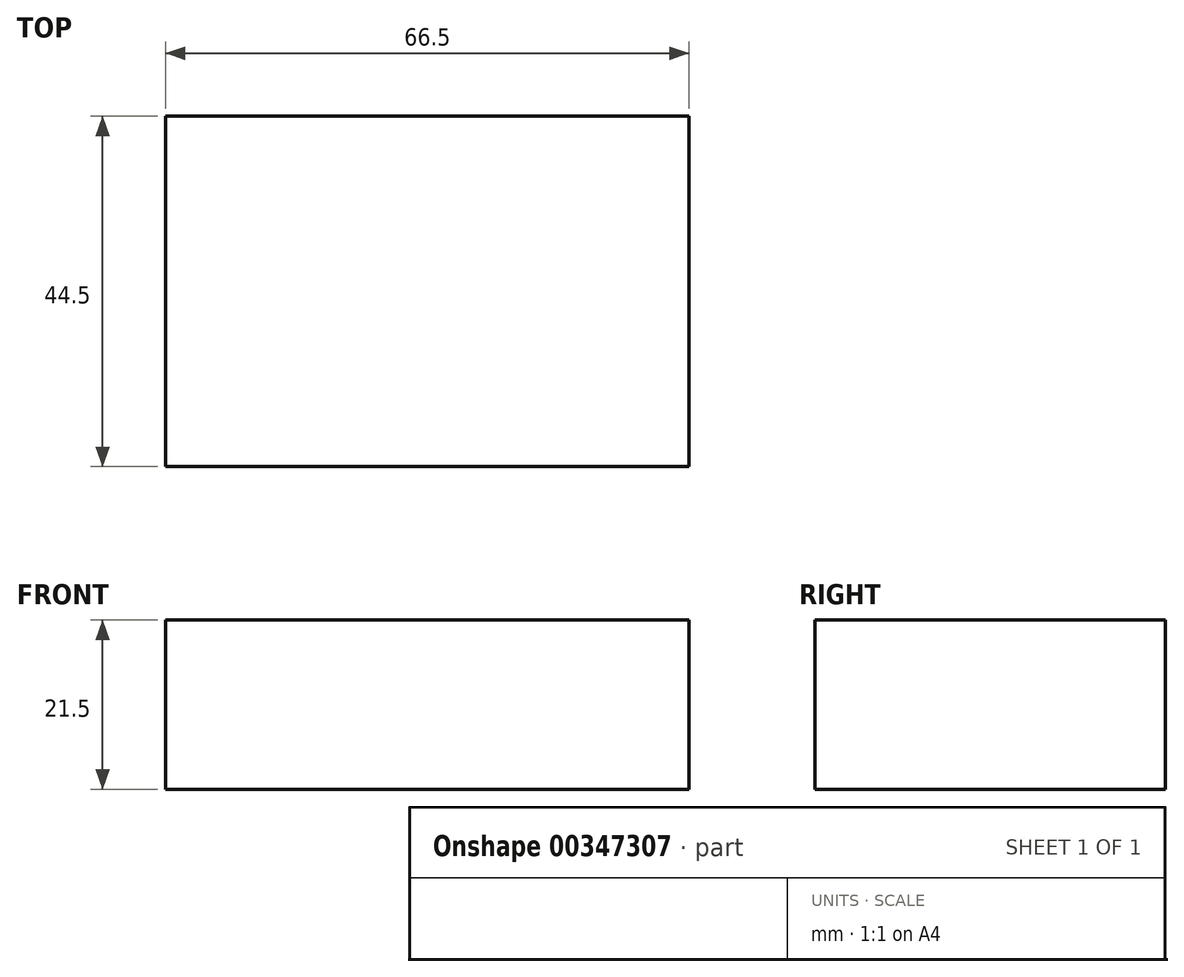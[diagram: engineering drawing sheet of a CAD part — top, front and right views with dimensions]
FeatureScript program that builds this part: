
annotation { "Feature Type Name" : "Feature", "Feature Type Description" : "" }
export const myFeature = defineFeature(function(context is Context, id is Id, definition is map)
    precondition{}
    {
        {
            var Q0;
            Q0=qCreatedBy(makeId("Top.planeOp"),FACE);
            var sketch = newSketch(context, id + "F0", { "sketchPlane" : qUnion([Q0])});
            skLineSegment(sketch, "E0.bottom", {"start": v(-31.82, 7.57) * mm, "end": v(34.68, 7.57) * mm});
            skLineSegment(sketch, "E0.top", {"start": v(-31.82, -36.93) * mm, "end": v(34.68, -36.93) * mm});
            skLineSegment(sketch, "E0.left", {"start": v(-31.82, 7.57) * mm, "end": v(-31.82, -36.93) * mm});
            skLineSegment(sketch, "E0.right", {"start": v(34.68, 7.57) * mm, "end": v(34.68, -36.93) * mm});
            skSolve(sketch);
        }
        {
            var Q0;
            Q0 = qSketchRegion(id + "F0", true);
            extrude(context, id + "F1", {"entities" : qUnion([Q0]), "depth" : 21.5 * mm});
        }
    });
